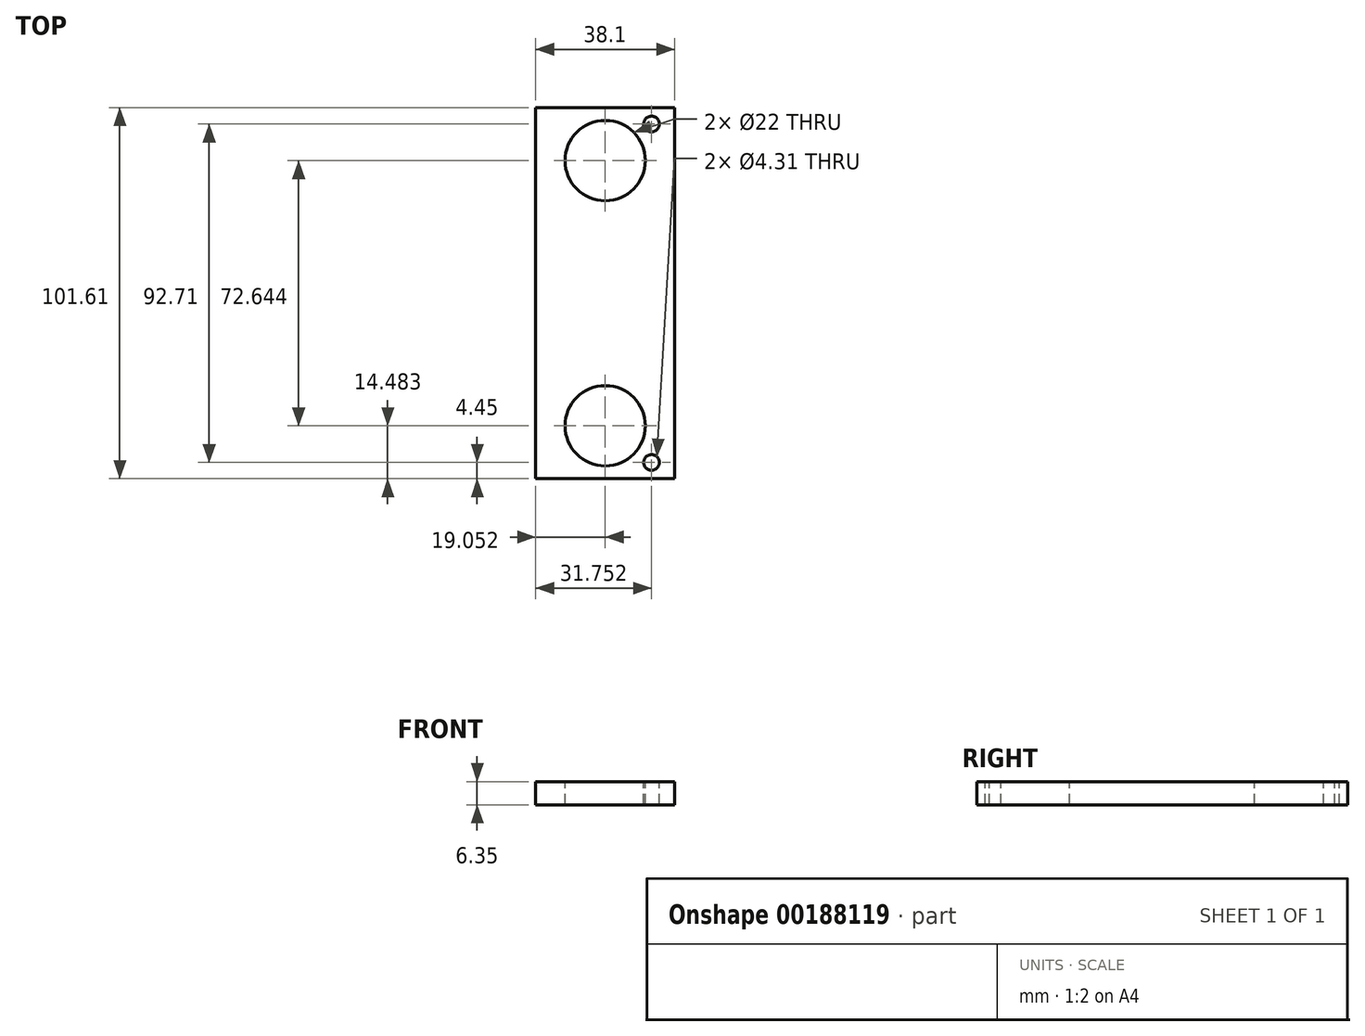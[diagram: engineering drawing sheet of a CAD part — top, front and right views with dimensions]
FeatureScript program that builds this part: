
annotation { "Feature Type Name" : "Feature", "Feature Type Description" : "" }
export const myFeature = defineFeature(function(context is Context, id is Id, definition is map)
    precondition{}
    {
        {
            var Q0;
            Q0=qCreatedBy(makeId("Top.planeOp"),FACE);
            var sketch = newSketch(context, id + "F0", { "sketchPlane" : qUnion([Q0])});
            skLineSegment(sketch, "E0.bottom", {"start": v(-71, -97.16) * mm, "end": v(-32.9, -97.16) * mm});
            skLineSegment(sketch, "E0.top", {"start": v(-71, 4.45) * mm, "end": v(-32.9, 4.45) * mm});
            skLineSegment(sketch, "E0.left", {"start": v(-71, -97.16) * mm, "end": v(-71, 4.45) * mm});
            skLineSegment(sketch, "E0.right", {"start": v(-32.9, -97.16) * mm, "end": v(-32.9, 4.45) * mm});
            skPoint(sketch, "E1", {"position": v(-51.95, -10.03) * mm});
            skPoint(sketch, "E2", {"position": v(-51.95, -82.68) * mm});
            skPoint(sketch, "E3", {"position": v(-39.25, 0) * mm});
            skPoint(sketch, "E4", {"position": v(-39.25, -92.7) * mm});
            skSolve(sketch);
        }
        {
            var Q0;
            Q0=makeQuery(id+"F0.imprint","IMPRINT",FACE,{"disambiguationData":[TD([[makeQuery(id+"F0.imprint","IMPRINT",EDGE,{"derivedFrom":sQuery(id+"F0.wireOp",EDGE,"E0.bottom")}),1.0]])]});
            extrude(context, id + "F1", {"entities" : qUnion([Q0]), "oppositeDirection" : true, "depth" : 6.35 * mm});
        }
        {
            var Q0;
            Q0=sQuery(id+"F0.wireOp",VERTEX,"E1");
            var Q1;
            Q1=sQuery(id+"F0.wireOp",VERTEX,"E2");
            var Q2;
            Q2=makeQuery(id+"F1.opExtrude","SWEPT_BODY",BODY,{"disambiguationData":[OSD([sQuery(id+"F0.wireOp",EDGE,"E0.bottom"),sQuery(id+"F0.wireOp",EDGE,"E0.top"),sQuery(id+"F0.wireOp",EDGE,"E0.left"),sQuery(id+"F0.wireOp",EDGE,"E0.right")])]});
            hole(context, id + "F2", {"style" : HoleStyle.SIMPLE, "endStyle" : HoleEndStyle.THROUGH, "standardTappedOrClearance" : lookupTablePath({ "standard" : "ISO", "fit" : "Normal", "size" : "M20", "type" : "Clearance" }), "standardBlindInLast" : lookupTablePath({ "fit" : "Standard", "standard" : "ISO", "size" : "M20", "type" : "Clearance" }), "holeDiameter" : 22 * mm, "startFromSketch" : true, "locations" : qUnion([Q0, Q1]), "scope" : qUnion([Q2]), "isTappedThrough" : true});
        }
        {
            var Q0;
            Q0=sQuery(id+"F0.wireOp",VERTEX,"E3");
            var Q1;
            Q1=sQuery(id+"F0.wireOp",VERTEX,"E4");
            var Q2;
            Q2=makeQuery(id+"F1.opExtrude","SWEPT_BODY",BODY,{"disambiguationData":[OSD([sQuery(id+"F0.wireOp",EDGE,"E0.bottom"),sQuery(id+"F0.wireOp",EDGE,"E0.top"),sQuery(id+"F0.wireOp",EDGE,"E0.left"),sQuery(id+"F0.wireOp",EDGE,"E0.right")])]});
            hole(context, id + "F3", {"style" : HoleStyle.SIMPLE, "endStyle" : HoleEndStyle.THROUGH, "holeDiameter" : 4.3 * mm, "startFromSketch" : true, "locations" : qUnion([Q0, Q1]), "scope" : qUnion([Q2]), "isTappedThrough" : true});
        }
    });
